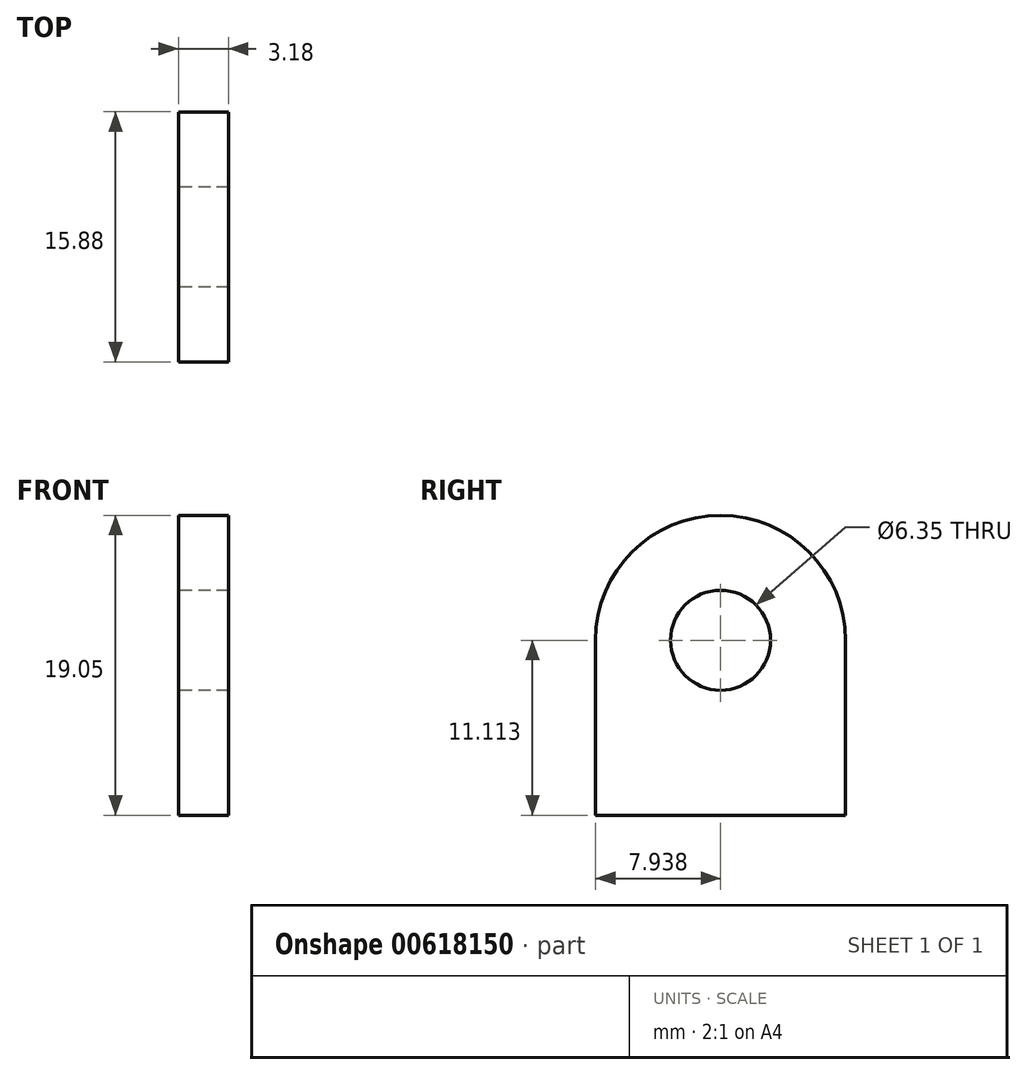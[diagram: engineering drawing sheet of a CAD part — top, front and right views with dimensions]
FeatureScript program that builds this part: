
annotation { "Feature Type Name" : "Feature", "Feature Type Description" : "" }
export const myFeature = defineFeature(function(context is Context, id is Id, definition is map)
    precondition{}
    {
        {
            var Q0;
            Q0=qCreatedBy(makeId("Right.planeOp"),FACE);
            var sketch = newSketch(context, id + "F0", { "sketchPlane" : qUnion([Q0])});
            skLineSegment(sketch, "E0.bottom", {"start": v(0, 0) * mm, "end": v(15.88, 0) * mm});
            skLineSegment(sketch, "E0.top", {"start": v(0, 11.11) * mm, "end": v(15.88, 11.11) * mm});
            skLineSegment(sketch, "E0.left", {"start": v(0, 0) * mm, "end": v(0, 11.11) * mm});
            skLineSegment(sketch, "E0.right", {"start": v(15.88, 0) * mm, "end": v(15.88, 11.11) * mm});
            skCircle(sketch, "E1", {"center": v(7.94, 11.11) * mm, "radius": 7.94 * mm});
            skCircle(sketch, "E2", {"center": v(7.94, 11.11) * mm, "radius": 3.18 * mm});
            skSolve(sketch);
        }
        {
            var Q0;
            Q0=qSketchRegion(id+"F0",true);
            extrude(context, id + "F1", {"entities" : qUnion([Q0]), "depth" : 3.17 * mm});
        }
    });
